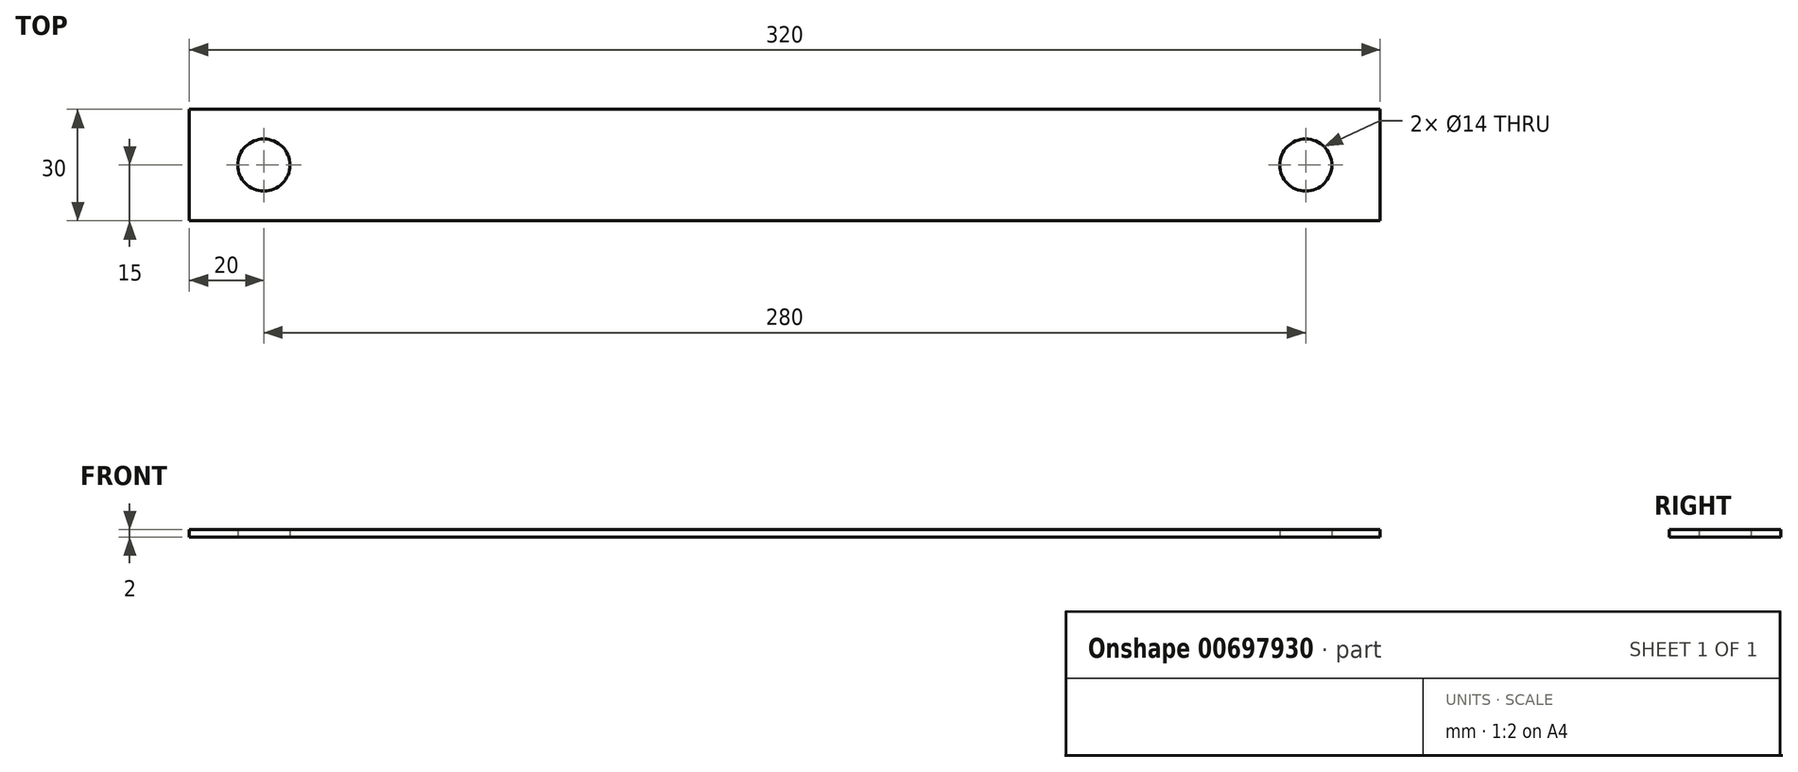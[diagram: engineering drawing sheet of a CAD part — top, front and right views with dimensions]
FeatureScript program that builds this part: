
annotation { "Feature Type Name" : "Feature", "Feature Type Description" : "" }
export const myFeature = defineFeature(function(context is Context, id is Id, definition is map)
    precondition{}
    {
        {
            var Q0;
            Q0=qCreatedBy(makeId("Top.planeOp"),FACE);
            var sketch = newSketch(context, id + "F0", { "sketchPlane" : qUnion([Q0])});
            skLineSegment(sketch, "E0.bottom", {"start": v(160, -15) * mm, "end": v(-160, -15) * mm});
            skLineSegment(sketch, "E0.top", {"start": v(160, 15) * mm, "end": v(-160, 15) * mm});
            skLineSegment(sketch, "E0.left", {"start": v(160, -15) * mm, "end": v(160, 15) * mm});
            skLineSegment(sketch, "E0.right", {"start": v(-160, -15) * mm, "end": v(-160, 15) * mm});
            skPoint(sketch, "E0.middle", {"position": v(0, 0) * mm});
            skSolve(sketch);
        }
        {
            var Q0;
            Q0=makeQuery(id+"F0.imprint","IMPRINT",FACE,{"disambiguationData":[TD([[makeQuery(id+"F0.imprint","IMPRINT",EDGE,{"derivedFrom":sQuery(id+"F0.wireOp",EDGE,"E0.bottom")}),-1.0]])]});
            var sketch = newSketch(context, id + "F1", { "sketchPlane" : qUnion([Q0])});
            skCircle(sketch, "E1", {"center": v(-140, 0) * mm, "radius": 7 * mm});
            skCircle(sketch, "E2", {"center": v(140, 0) * mm, "radius": 7 * mm});
            skSolve(sketch);
        }
        {
            var Q0;
            Q0=makeQuery(id+"F1.imprint","IMPRINT",FACE,{"disambiguationData":[TD([[makeQuery(id+"F1.imprint","IMPRINT",EDGE,{"derivedFrom":sQuery(id+"F1.wireOp",EDGE,"E1")}),-1.0]])]});
            extrude(context, id + "F2", {"entities" : qUnion([Q0]), "endBound" : BoundingType.SYMMETRIC, "depth" : 2 * mm, "offsetDistance" : 25 * mm});
        }
    });
